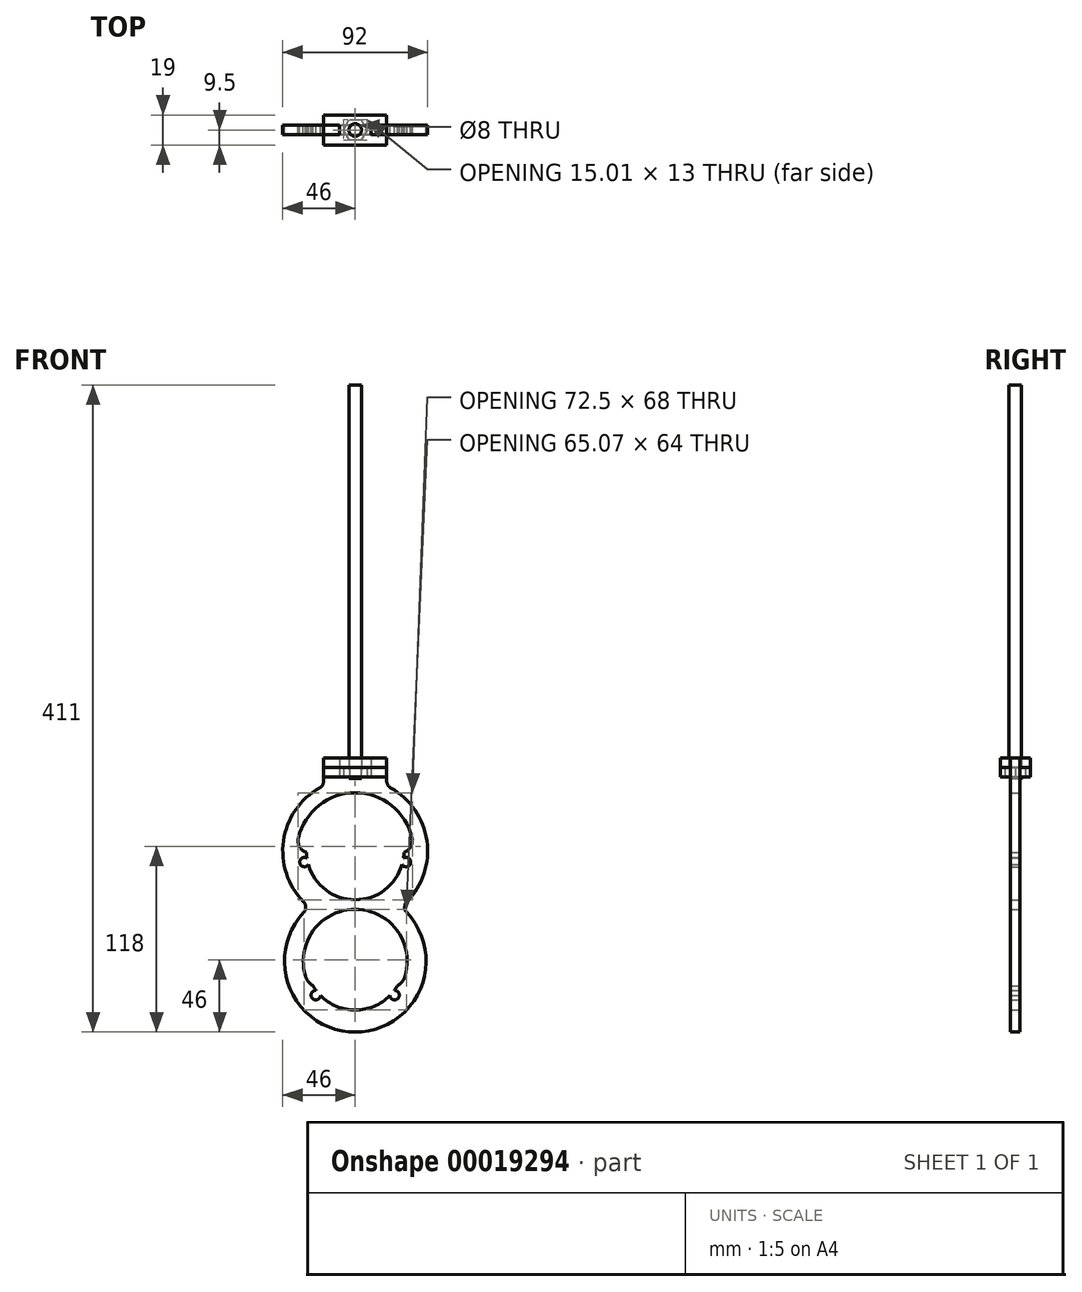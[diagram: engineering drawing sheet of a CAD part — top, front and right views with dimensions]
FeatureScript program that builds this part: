
annotation { "Feature Type Name" : "Feature", "Feature Type Description" : "" }
export const myFeature = defineFeature(function(context is Context, id is Id, definition is map)
    precondition{}
    {
        {
            var Q0;
            Q0=qCreatedBy(makeId("Front.planeOp"),FACE);
            var sketch = newSketch(context, id + "F0", { "sketchPlane" : qUnion([Q0])});
            skCircle(sketch, "E0", {"center": v(0, 0) * mm, "radius": 30 * mm, "construction": true});
            skArc(sketch, "E1", {"start": v(-30.68, -4.44) * mm, "mid": v(-35.18, -7.63) * mm, "end": v(-29.76, -8.67) * mm});
            skArc(sketch, "E2", {"start": v(32.83, -32.22) * mm, "mid": v(0, 46) * mm, "end": v(-32.83, -32.22) * mm});
            skArc(sketch, "E3", {"start": v(-29.76, -8.67) * mm, "mid": v(0, -31) * mm, "end": v(29.76, -8.67) * mm});
            skArc(sketch, "E4.trimOffspring", {"start": v(30.68, -4.44) * mm, "mid": v(30.88, -2.72) * mm, "end": v(30.98, -1) * mm});
            skArc(sketch, "E5.trimOffspring", {"start": v(29.76, -8.67) * mm, "mid": v(35.18, -7.63) * mm, "end": v(30.68, -4.44) * mm});
            skArc(sketch, "E6.trimOffspring", {"start": v(36.05, 8.33) * mm, "mid": v(0, 37) * mm, "end": v(-36.05, 8.33) * mm});
            skArc(sketch, "E7", {"start": v(-36.05, 8.33) * mm, "mid": v(-35.28, 2.7) * mm, "end": v(-30.98, -1) * mm});
            skLineSegment(sketch, "E8", {"start": v(0, -7) * mm, "end": v(0, 0) * mm, "construction": true});
            skArc(sketch, "E9.0.MirrorCS", {"start": v(36.05, 8.33) * mm, "mid": v(35.28, 2.7) * mm, "end": v(30.98, -1) * mm});
            skArc(sketch, "E10.trimOffspring", {"start": v(-30.98, -1) * mm, "mid": v(-30.88, -2.72) * mm, "end": v(-30.68, -4.44) * mm});
            skLineSegment(sketch, "E11", {"start": v(0, 37) * mm, "end": v(0, 46) * mm, "construction": true});
            skLineSegment(sketch, "E12", {"start": v(-30.98, -1) * mm, "end": v(30.98, -1) * mm, "construction": true});
            skLineSegment(sketch, "E13", {"start": v(-32.25, -7) * mm, "end": v(32.25, -7) * mm, "construction": true});
            skCircle(sketch, "E14", {"center": v(0, -70) * mm, "radius": 30 * mm, "construction": true});
            skArc(sketch, "E15", {"start": v(-22.01, -91.83) * mm, "mid": v(0, -101) * mm, "end": v(22.01, -91.83) * mm});
            skArc(sketch, "E16", {"start": v(-32.76, -39.15) * mm, "mid": v(0, -115) * mm, "end": v(32.76, -39.15) * mm});
            skLineSegment(sketch, "E17", {"start": v(0, -70) * mm, "end": v(0, -39) * mm, "construction": true});
            skLineSegment(sketch, "E18", {"start": v(0, -70) * mm, "end": v(45, -70) * mm, "construction": true});
            skArc(sketch, "E19", {"start": v(-24.84, -88.54) * mm, "mid": v(-27.18, -93.6) * mm, "end": v(-22, -91.54) * mm});
            skArc(sketch, "E20", {"start": v(22, -91.54) * mm, "mid": v(27.18, -93.6) * mm, "end": v(24.84, -88.54) * mm});
            skLineSegment(sketch, "E21", {"start": v(-25, -91.54) * mm, "end": v(25, -91.54) * mm, "construction": true});
            skArc(sketch, "E22", {"start": v(31.53, -79.75) * mm, "mid": v(0, -37) * mm, "end": v(-31.53, -79.75) * mm});
            skArc(sketch, "E23", {"start": v(-31.53, -79.75) * mm, "mid": v(-29.74, -83.1) * mm, "end": v(-26.82, -85.54) * mm});
            skArc(sketch, "E24.0.MirrorCS", {"start": v(31.53, -79.75) * mm, "mid": v(29.74, -83.1) * mm, "end": v(26.82, -85.54) * mm});
            skArc(sketch, "E25.trimOffspring", {"start": v(24.84, -88.54) * mm, "mid": v(25.88, -87.07) * mm, "end": v(26.82, -85.54) * mm});
            skArc(sketch, "E26.trimOffspring", {"start": v(-26.82, -85.54) * mm, "mid": v(-25.88, -87.07) * mm, "end": v(-24.84, -88.54) * mm});
            skLineSegment(sketch, "E27", {"start": v(-26.82, -85.54) * mm, "end": v(26.82, -85.54) * mm, "construction": true});
            skPoint(sketch, "E28.visualSharp", {"position": v(-29.07, -35.65) * mm});
            skArc(sketch, "E28.filletArc", {"start": v(-32.76, -39.15) * mm, "mid": v(-31.4, -35.67) * mm, "end": v(-32.83, -32.22) * mm});
            skPoint(sketch, "E29.visualSharp", {"position": v(29.07, -35.65) * mm});
            skArc(sketch, "E29.filletArc", {"start": v(32.83, -32.22) * mm, "mid": v(31.4, -35.67) * mm, "end": v(32.76, -39.15) * mm});
            skLineSegment(sketch, "E30", {"start": v(-20, 41.42) * mm, "end": v(-20, 59) * mm});
            skLineSegment(sketch, "E31", {"start": v(-20, 59) * mm, "end": v(-10, 59) * mm});
            skLineSegment(sketch, "E32", {"start": v(20, 59) * mm, "end": v(20, 41.42) * mm});
            skLineSegment(sketch, "E33", {"start": v(-10, 59) * mm, "end": v(-10, 47) * mm});
            skLineSegment(sketch, "E34", {"start": v(-10, 47) * mm, "end": v(-4, 47) * mm});
            skLineSegment(sketch, "E35", {"start": v(-4, 47) * mm, "end": v(-4, 46) * mm});
            skLineSegment(sketch, "E36", {"start": v(-4, 46) * mm, "end": v(4, 46) * mm});
            skLineSegment(sketch, "E37", {"start": v(10, 47) * mm, "end": v(10, 59) * mm});
            skLineSegment(sketch, "E38.trimOffspring", {"start": v(10, 59) * mm, "end": v(20, 59) * mm});
            skLineSegment(sketch, "E39", {"start": v(4, 46) * mm, "end": v(4, 47) * mm});
            skLineSegment(sketch, "E40", {"start": v(4, 47) * mm, "end": v(10, 47) * mm});
            skSolve(sketch);
        }
        {
            var Q0;
            Q0=qSketchRegion(id+"F0",true);
            extrude(context, id + "F1", {"entities" : qUnion([Q0]), "depth" : 6 * mm});
        }
        {
            var Q0;
            Q0=makeQuery(id+"F1.opExtrude","SWEPT_FACE",FACE,{"disambiguationData":[OSD([sQuery(id+"F0.wireOp",EDGE,"E36")])]});
            var sketch = newSketch(context, id + "F2", { "sketchPlane" : qUnion([Q0])});
            skCircle(sketch, "E41", {"center": v(0, -3) * mm, "radius": 4 * mm});
            skSolve(sketch);
        }
        {
            var Q0;
            Q0=qSketchRegion(id+"F2",true);
            extrude(context, id + "F3", {"entities" : qUnion([Q0]), "depth" : 250 * mm});
        }
        {
            var Q0;
            Q0=makeQuery(id+"F1.opExtrude","SWEPT_FACE",FACE,{"disambiguationData":[OSD([sQuery(id+"F0.wireOp",EDGE,"E40")])]});
            var sketch = newSketch(context, id + "F4", { "sketchPlane" : qUnion([Q0])});
            skLineSegment(sketch, "E42", {"start": v(-20, 0) * mm, "end": v(-20, 6.5) * mm});
            skLineSegment(sketch, "E43", {"start": v(-20, 6.5) * mm, "end": v(20, 6.5) * mm});
            skLineSegment(sketch, "E44", {"start": v(20, 6.5) * mm, "end": v(20, 0) * mm});
            skLineSegment(sketch, "E45", {"start": v(20, 0) * mm, "end": v(10, 0) * mm});
            skLineSegment(sketch, "E46", {"start": v(10, 0) * mm, "end": v(10, -6) * mm});
            skLineSegment(sketch, "E47", {"start": v(10, -6) * mm, "end": v(20, -6) * mm});
            skLineSegment(sketch, "E48", {"start": v(20, -6) * mm, "end": v(20, -12.5) * mm});
            skLineSegment(sketch, "E49", {"start": v(20, -12.5) * mm, "end": v(-20, -12.5) * mm});
            skLineSegment(sketch, "E50", {"start": v(-20, -12.5) * mm, "end": v(-20, -6) * mm});
            skLineSegment(sketch, "E51", {"start": v(-20, -6) * mm, "end": v(-10, -6) * mm});
            skLineSegment(sketch, "E52", {"start": v(-10, -6) * mm, "end": v(-10, 0) * mm});
            skLineSegment(sketch, "E53", {"start": v(-10, 0) * mm, "end": v(-20, 0) * mm});
            skCircle(sketch, "E54.cCircle", {"center": v(0, -3) * mm, "radius": 6.5 * mm, "construction": true});
            skLineSegment(sketch, "E54.0", {"start": v(-3.75, 3.5) * mm, "end": v(3.75, 3.5) * mm});
            skLineSegment(sketch, "E54.1", {"start": v(3.75, 3.5) * mm, "end": v(7.5, -3) * mm});
            skLineSegment(sketch, "E54.2", {"start": v(7.5, -3) * mm, "end": v(3.75, -9.5) * mm});
            skLineSegment(sketch, "E54.3", {"start": v(3.75, -9.5) * mm, "end": v(-3.75, -9.5) * mm});
            skLineSegment(sketch, "E54.4", {"start": v(-3.75, -9.5) * mm, "end": v(-7.5, -3) * mm});
            skLineSegment(sketch, "E54.5", {"start": v(-7.5, -3) * mm, "end": v(-3.75, 3.5) * mm});
            skPoint(sketch, "E54.0.midPoint", {"position": v(0, 3.5) * mm});
            skSolve(sketch);
        }
        {
            var Q0;
            Q0=qSketchRegion(id+"F4",true);
            extrude(context, id + "F5", {"entities" : qUnion([Q0]), "depth" : 6 * mm});
        }
        {
            var Q0;
            Q0=makeQuery(id+"F5.opExtrude","CAP_FACE",FACE,{"disambiguationData":[OSD([sQuery(id+"F4.wireOp",EDGE,"E42"),sQuery(id+"F4.wireOp",EDGE,"E43"),sQuery(id+"F4.wireOp",EDGE,"E44"),sQuery(id+"F4.wireOp",EDGE,"E45"),sQuery(id+"F4.wireOp",EDGE,"E46"),sQuery(id+"F4.wireOp",EDGE,"E47"),sQuery(id+"F4.wireOp",EDGE,"E48"),sQuery(id+"F4.wireOp",EDGE,"E49"),sQuery(id+"F4.wireOp",EDGE,"E50"),sQuery(id+"F4.wireOp",EDGE,"E51"),sQuery(id+"F4.wireOp",EDGE,"E52"),sQuery(id+"F4.wireOp",EDGE,"E53"),sQuery(id+"F4.wireOp",EDGE,"E54.0"),sQuery(id+"F4.wireOp",EDGE,"E54.1"),sQuery(id+"F4.wireOp",EDGE,"E54.2"),sQuery(id+"F4.wireOp",EDGE,"E54.3"),sQuery(id+"F4.wireOp",EDGE,"E54.4"),sQuery(id+"F4.wireOp",EDGE,"E54.5")])],"isStart":false});
            var sketch = newSketch(context, id + "F6", { "sketchPlane" : qUnion([Q0])});
            skSolve(sketch);
        }
        {
            var Q0;
            Q0=makeQuery(id+"F6.imprint","IMPRINT",FACE,{"disambiguationData":[TD([[makeQuery(id+"F6.imprint","IMPRINT",EDGE,{"derivedFrom":makeQuery(id+"F5.opExtrude","CAP_EDGE",EDGE,{"disambiguationData":[OSD([sQuery(id+"F4.wireOp",EDGE,"E42")])],"isStart":false})}),-1.0]])]});
            var sketch = newSketch(context, id + "F7", { "sketchPlane" : qUnion([Q0])});
            skLineSegment(sketch, "E55.0.0", {"start": v(20, -6) * mm, "end": v(10, -6) * mm});
            skLineSegment(sketch, "E55.0.1", {"start": v(10, -6) * mm, "end": v(10, 0) * mm});
            skLineSegment(sketch, "E55.0.2", {"start": v(10, 0) * mm, "end": v(20, 0) * mm});
            skLineSegment(sketch, "E55.0.3", {"start": v(20, 0) * mm, "end": v(20, 6.5) * mm});
            skLineSegment(sketch, "E55.0.4", {"start": v(20, 6.5) * mm, "end": v(-20, 6.5) * mm});
            skLineSegment(sketch, "E55.0.5", {"start": v(-20, 6.5) * mm, "end": v(-20, 0) * mm});
            skLineSegment(sketch, "E55.0.6", {"start": v(-20, 0) * mm, "end": v(-10, 0) * mm});
            skLineSegment(sketch, "E55.0.7", {"start": v(-10, 0) * mm, "end": v(-10, -6) * mm});
            skLineSegment(sketch, "E55.0.8", {"start": v(-10, -6) * mm, "end": v(-20, -6) * mm});
            skLineSegment(sketch, "E55.0.9", {"start": v(-20, -6) * mm, "end": v(-20, -12.5) * mm});
            skLineSegment(sketch, "E55.0.10", {"start": v(-20, -12.5) * mm, "end": v(20, -12.5) * mm});
            skLineSegment(sketch, "E55.0.11", {"start": v(20, -12.5) * mm, "end": v(20, -6) * mm});
            skCircle(sketch, "E56.0", {"center": v(0, -3) * mm, "radius": 4 * mm});
            skSolve(sketch);
        }
        {
            var Q0;
            Q0=qSketchRegion(id+"F7",true);
            extrude(context, id + "F8", {"entities" : qUnion([Q0]), "depth" : 6 * mm});
        }
        {
            var Q0;
            Q0=makeQuery(id+"F1.opExtrude","SWEPT_EDGE",EDGE,{"disambiguationData":[OSD([sQuery(id+"F0.wireOp",EDGE,"E2"),sQuery(id+"F0.wireOp",EDGE,"E30")])]});
            var Q1;
            Q1=makeQuery(id+"F1.opExtrude","SWEPT_EDGE",EDGE,{"disambiguationData":[OSD([sQuery(id+"F0.wireOp",EDGE,"E2"),sQuery(id+"F0.wireOp",EDGE,"E32")])]});
            fillet(context, id + "F9", {"entities" : qUnion([Q0, Q1]), "radius" : 5 * mm, "tangentPropagation" : true, "allowEdgeOverflow" : false});
        }
    });
